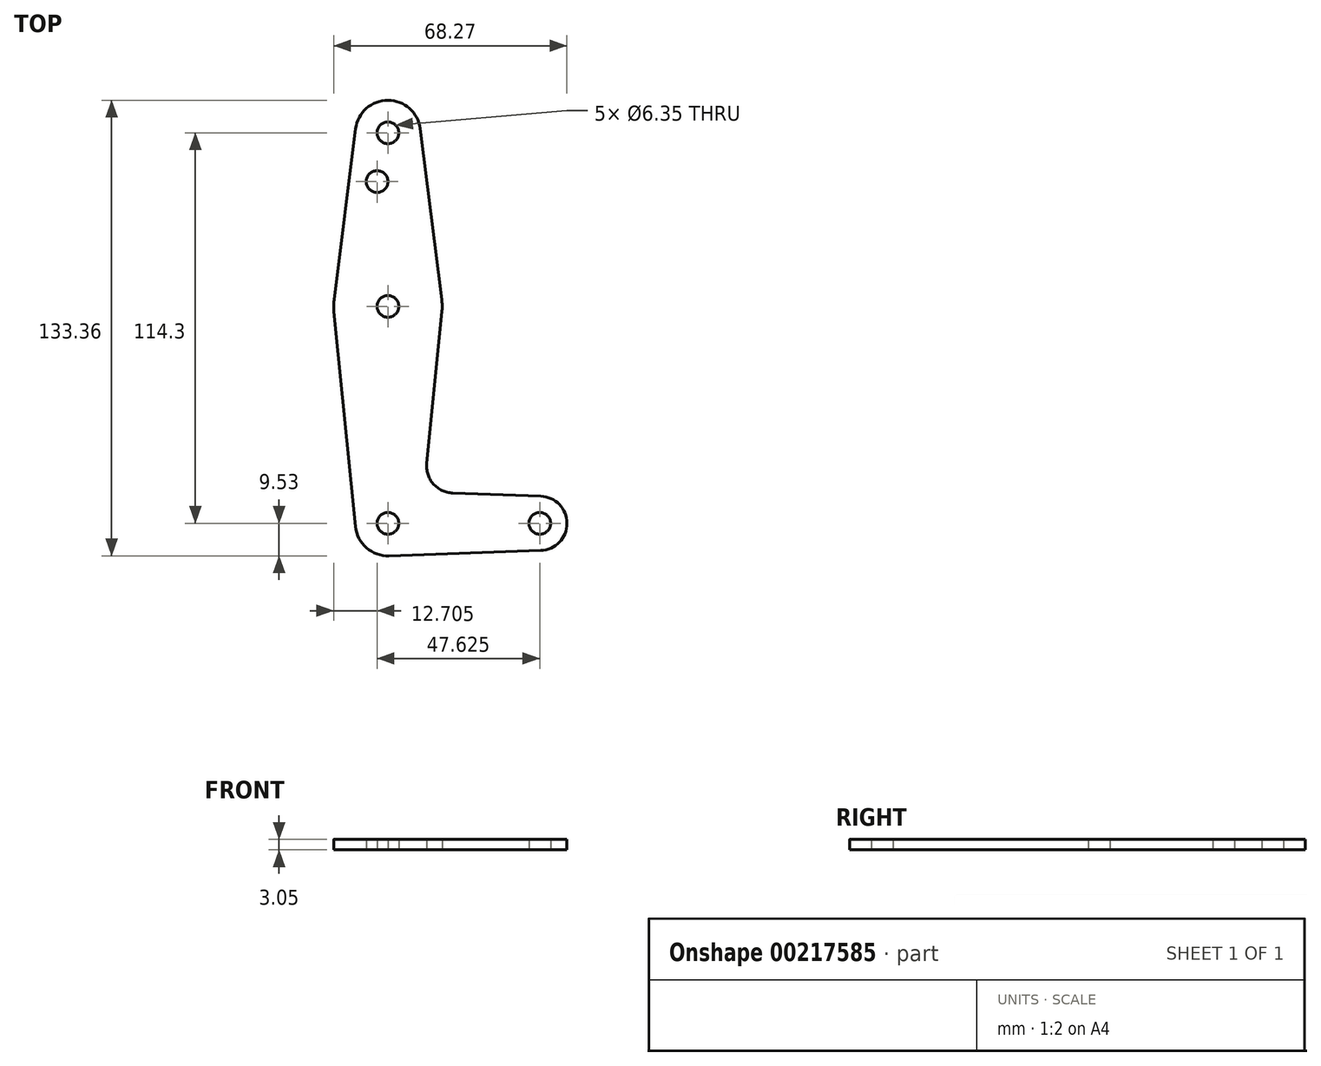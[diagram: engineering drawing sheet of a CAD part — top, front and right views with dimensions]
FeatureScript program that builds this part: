
annotation { "Feature Type Name" : "Feature", "Feature Type Description" : "" }
export const myFeature = defineFeature(function(context is Context, id is Id, definition is map)
    precondition{}
    {
        {
            var Q0;
            Q0=qCreatedBy(makeId("Top.planeOp"),FACE);
            var sketch = newSketch(context, id + "F0", { "sketchPlane" : qUnion([Q0])});
            skCircle(sketch, "E0", {"center": v(0, 0) * mm, "radius": 9.52 * mm});
            skCircle(sketch, "E1", {"center": v(0, 63.5) * mm, "radius": 15.88 * mm});
            skCircle(sketch, "E2", {"center": v(0, 114.3) * mm, "radius": 9.53 * mm});
            skCircle(sketch, "E3", {"center": v(44.45, 0) * mm, "radius": 7.94 * mm});
            skLineSegment(sketch, "E4", {"start": v(-15.8, 61.91) * mm, "end": v(-9.48, -0.95) * mm});
            skLineSegment(sketch, "E5", {"start": v(-15.75, 65.48) * mm, "end": v(-9.45, 115.5) * mm});
            skLineSegment(sketch, "E6", {"start": v(15.75, 65.48) * mm, "end": v(9.45, 115.5) * mm});
            skLineSegment(sketch, "E7", {"start": v(0.34, -9.52) * mm, "end": v(44.73, -7.94) * mm});
            skCircle(sketch, "E8", {"center": v(0, 114.3) * mm, "radius": 3.18 * mm});
            skCircle(sketch, "E9", {"center": v(0, 63.5) * mm, "radius": 3.18 * mm});
            skCircle(sketch, "E10", {"center": v(0, 0) * mm, "radius": 3.18 * mm});
            skCircle(sketch, "E11", {"center": v(44.45, 0) * mm, "radius": 3.18 * mm});
            skLineSegment(sketch, "E12", {"start": v(0, 0) * mm, "end": v(44.45, 0) * mm, "construction": true});
            skLineSegment(sketch, "E13", {"start": v(0, 0) * mm, "end": v(0, 114.3) * mm, "construction": true});
            skCircle(sketch, "E14", {"center": v(-3.18, 100.03) * mm, "radius": 3.18 * mm});
            skLineSegment(sketch, "E15", {"start": v(15.8, 61.91) * mm, "end": v(11.34, 17.6) * mm});
            skLineSegment(sketch, "E16", {"start": v(44.73, 7.94) * mm, "end": v(18.97, 8.86) * mm});
            skArc(sketch, "E17.filletArc", {"start": v(11.34, 17.6) * mm, "mid": v(13.26, 11.57) * mm, "end": v(18.97, 8.86) * mm});
            skSolve(sketch);
        }
        {
            var Q0;
            Q0 = qSketchRegion(id + "F0", true);
            extrude(context, id + "F1", {"entities" : qUnion([Q0]), "depth" : 3.05 * mm});
        }
    });
